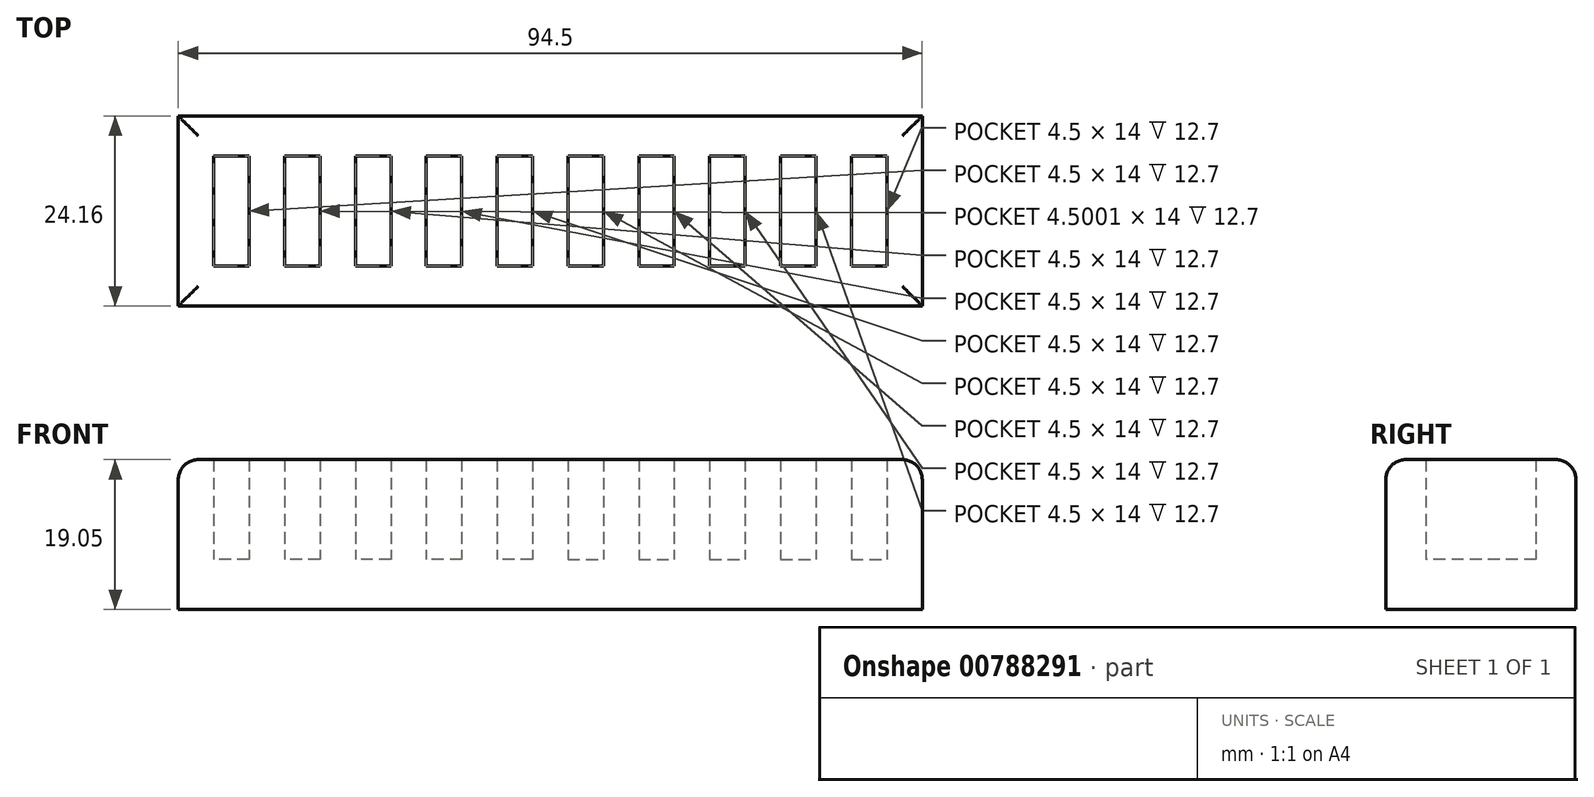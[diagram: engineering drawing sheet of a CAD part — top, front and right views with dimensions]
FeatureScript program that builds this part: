
annotation { "Feature Type Name" : "Feature", "Feature Type Description" : "" }
export const myFeature = defineFeature(function(context is Context, id is Id, definition is map)
    precondition{}
    {
        {
            var Q0;
            Q0=qCreatedBy(makeId("Top.planeOp"),FACE);
            var sketch = newSketch(context, id + "F0", { "sketchPlane" : qUnion([Q0])});
            skLineSegment(sketch, "E0.bottom", {"start": v(-24.19, 0) * mm, "end": v(-15.19, 0) * mm});
            skLineSegment(sketch, "E0.top", {"start": v(-24.19, 24.16) * mm, "end": v(-15.19, 24.16) * mm});
            skLineSegment(sketch, "E0.left", {"start": v(-24.19, 0) * mm, "end": v(-24.19, 24.16) * mm});
            skLineSegment(sketch, "E0.right", {"start": v(-15.19, 0) * mm, "end": v(-15.19, 24.16) * mm});
            skLineSegment(sketch, "E1", {"start": v(-15.19, 24.16) * mm, "end": v(-15.19, 19.08) * mm});
            skLineSegment(sketch, "E2.bottom", {"start": v(-24.19, 0) * mm, "end": v(-19.69, 0) * mm});
            skLineSegment(sketch, "E2.top", {"start": v(-24.19, 5.08) * mm, "end": v(-19.69, 5.08) * mm});
            skLineSegment(sketch, "E2.left", {"start": v(-24.19, 0) * mm, "end": v(-24.19, 5.08) * mm});
            skLineSegment(sketch, "E2.right", {"start": v(-19.69, 0) * mm, "end": v(-19.69, 5.08) * mm});
            skLineSegment(sketch, "E3.bottom", {"start": v(-19.69, 5.08) * mm, "end": v(-15.19, 5.08) * mm});
            skLineSegment(sketch, "E3.top", {"start": v(-19.69, 19.08) * mm, "end": v(-15.19, 19.08) * mm});
            skLineSegment(sketch, "E3.left", {"start": v(-19.69, 5.08) * mm, "end": v(-19.69, 19.08) * mm});
            skLineSegment(sketch, "E3.right", {"start": v(-15.19, 5.08) * mm, "end": v(-15.19, 19.08) * mm});
            skLineSegment(sketch, "E4", {"start": v(-24.19, 0) * mm, "end": v(-33.19, 0) * mm});
            skLineSegment(sketch, "E5", {"start": v(-33.19, 0) * mm, "end": v(-42.19, 0) * mm});
            skLineSegment(sketch, "E6", {"start": v(-42.19, 0) * mm, "end": v(-51.19, 0) * mm});
            skLineSegment(sketch, "E7", {"start": v(-51.19, 0) * mm, "end": v(-60.19, 0) * mm});
            skLineSegment(sketch, "E8", {"start": v(-60.19, 0) * mm, "end": v(-69.19, 0) * mm});
            skLineSegment(sketch, "E9", {"start": v(-15.19, 0) * mm, "end": v(-6.19, 0) * mm});
            skLineSegment(sketch, "E10", {"start": v(-6.19, 0) * mm, "end": v(2.81, 0) * mm});
            skLineSegment(sketch, "E11", {"start": v(2.81, 0) * mm, "end": v(11.81, 0) * mm});
            skLineSegment(sketch, "E12", {"start": v(11.81, 0) * mm, "end": v(20.81, 0) * mm});
            skLineSegment(sketch, "E13.bottom", {"start": v(-24.19, 24.16) * mm, "end": v(-33.19, 24.16) * mm});
            skLineSegment(sketch, "E13.left", {"start": v(-24.19, 24.16) * mm, "end": v(-24.19, 0) * mm});
            skLineSegment(sketch, "E13.right", {"start": v(-33.19, 24.16) * mm, "end": v(-33.19, 0) * mm});
            skLineSegment(sketch, "E14.bottom", {"start": v(-33.19, 24.16) * mm, "end": v(-42.19, 24.16) * mm});
            skLineSegment(sketch, "E14.right", {"start": v(-42.19, 24.16) * mm, "end": v(-42.19, 0) * mm});
            skLineSegment(sketch, "E15.bottom", {"start": v(-42.19, 24.16) * mm, "end": v(-51.19, 24.16) * mm});
            skLineSegment(sketch, "E15.right", {"start": v(-51.19, 24.16) * mm, "end": v(-51.19, 0) * mm});
            skLineSegment(sketch, "E16.bottom", {"start": v(-51.19, 24.16) * mm, "end": v(-60.19, 24.16) * mm});
            skLineSegment(sketch, "E16.right", {"start": v(-60.19, 24.16) * mm, "end": v(-60.19, 0) * mm});
            skLineSegment(sketch, "E17.bottom", {"start": v(-60.19, 24.16) * mm, "end": v(-69.19, 24.16) * mm});
            skLineSegment(sketch, "E17.right", {"start": v(-69.19, 24.16) * mm, "end": v(-69.19, 0) * mm});
            skLineSegment(sketch, "E18.bottom", {"start": v(-15.19, 24.16) * mm, "end": v(-6.19, 24.16) * mm});
            skLineSegment(sketch, "E18.left", {"start": v(-15.19, 24.16) * mm, "end": v(-15.19, 0) * mm});
            skLineSegment(sketch, "E18.right", {"start": v(-6.19, 24.16) * mm, "end": v(-6.19, 0) * mm});
            skLineSegment(sketch, "E19.bottom", {"start": v(-6.19, 24.16) * mm, "end": v(2.81, 24.16) * mm});
            skLineSegment(sketch, "E19.right", {"start": v(2.81, 24.16) * mm, "end": v(2.81, 0) * mm});
            skLineSegment(sketch, "E20.bottom", {"start": v(2.81, 24.16) * mm, "end": v(11.81, 24.16) * mm});
            skLineSegment(sketch, "E20.right", {"start": v(11.81, 24.16) * mm, "end": v(11.81, 0) * mm});
            skLineSegment(sketch, "E21.bottom", {"start": v(11.81, 24.16) * mm, "end": v(20.81, 24.16) * mm});
            skLineSegment(sketch, "E21.right", {"start": v(20.81, 24.16) * mm, "end": v(20.81, 0) * mm});
            skLineSegment(sketch, "E22", {"start": v(-15.19, 19.08) * mm, "end": v(-6.19, 19.08) * mm});
            skLineSegment(sketch, "E23", {"start": v(-6.19, 19.08) * mm, "end": v(2.81, 19.08) * mm});
            skLineSegment(sketch, "E24", {"start": v(2.81, 19.08) * mm, "end": v(11.81, 19.08) * mm});
            skLineSegment(sketch, "E25", {"start": v(11.81, 19.08) * mm, "end": v(20.81, 19.08) * mm});
            skLineSegment(sketch, "E26", {"start": v(-19.69, 19.08) * mm, "end": v(-33.19, 19.08) * mm});
            skLineSegment(sketch, "E27", {"start": v(-33.19, 19.08) * mm, "end": v(-42.19, 19.08) * mm});
            skLineSegment(sketch, "E28", {"start": v(-42.19, 19.08) * mm, "end": v(-51.19, 19.08) * mm});
            skLineSegment(sketch, "E29", {"start": v(-51.19, 19.08) * mm, "end": v(-60.19, 19.08) * mm});
            skLineSegment(sketch, "E30", {"start": v(-60.19, 19.08) * mm, "end": v(-69.19, 19.08) * mm});
            skLineSegment(sketch, "E31", {"start": v(-15.19, 5.08) * mm, "end": v(-6.19, 5.08) * mm});
            skLineSegment(sketch, "E32", {"start": v(-6.19, 5.08) * mm, "end": v(2.81, 5.08) * mm});
            skLineSegment(sketch, "E33", {"start": v(2.81, 5.08) * mm, "end": v(11.81, 5.08) * mm});
            skLineSegment(sketch, "E34", {"start": v(11.81, 5.08) * mm, "end": v(20.81, 5.08) * mm});
            skLineSegment(sketch, "E35", {"start": v(-24.19, 5.08) * mm, "end": v(-33.19, 5.08) * mm});
            skLineSegment(sketch, "E36", {"start": v(-33.19, 5.08) * mm, "end": v(-42.19, 5.08) * mm});
            skLineSegment(sketch, "E37", {"start": v(-42.19, 5.08) * mm, "end": v(-51.19, 5.08) * mm});
            skLineSegment(sketch, "E38", {"start": v(-51.19, 5.08) * mm, "end": v(-60.19, 5.08) * mm});
            skLineSegment(sketch, "E39", {"start": v(-60.19, 5.08) * mm, "end": v(-69.19, 5.08) * mm});
            skLineSegment(sketch, "E40.bottom", {"start": v(-60.19, 19.08) * mm, "end": v(-64.69, 19.08) * mm});
            skLineSegment(sketch, "E40.top", {"start": v(-60.19, 5.08) * mm, "end": v(-64.69, 5.08) * mm});
            skLineSegment(sketch, "E40.left", {"start": v(-60.19, 19.08) * mm, "end": v(-60.19, 5.08) * mm});
            skLineSegment(sketch, "E40.right", {"start": v(-64.69, 19.08) * mm, "end": v(-64.69, 5.08) * mm});
            skLineSegment(sketch, "E41.bottom", {"start": v(-51.19, 19.08) * mm, "end": v(-55.69, 19.08) * mm});
            skLineSegment(sketch, "E41.top", {"start": v(-51.19, 5.08) * mm, "end": v(-55.69, 5.08) * mm});
            skLineSegment(sketch, "E41.left", {"start": v(-51.19, 19.08) * mm, "end": v(-51.19, 5.08) * mm});
            skLineSegment(sketch, "E41.right", {"start": v(-55.69, 19.08) * mm, "end": v(-55.69, 5.08) * mm});
            skLineSegment(sketch, "E42.bottom", {"start": v(-42.19, 19.08) * mm, "end": v(-46.69, 19.08) * mm});
            skLineSegment(sketch, "E42.top", {"start": v(-42.19, 5.08) * mm, "end": v(-46.69, 5.08) * mm});
            skLineSegment(sketch, "E42.left", {"start": v(-42.19, 19.08) * mm, "end": v(-42.19, 5.08) * mm});
            skLineSegment(sketch, "E42.right", {"start": v(-46.69, 19.08) * mm, "end": v(-46.69, 5.08) * mm});
            skLineSegment(sketch, "E43.bottom", {"start": v(-33.19, 19.08) * mm, "end": v(-37.69, 19.08) * mm});
            skLineSegment(sketch, "E43.top", {"start": v(-33.19, 5.08) * mm, "end": v(-37.69, 5.08) * mm});
            skLineSegment(sketch, "E43.left", {"start": v(-33.19, 19.08) * mm, "end": v(-33.19, 5.08) * mm});
            skLineSegment(sketch, "E43.right", {"start": v(-37.69, 19.08) * mm, "end": v(-37.69, 5.08) * mm});
            skLineSegment(sketch, "E44.bottom", {"start": v(-24.19, 19.08) * mm, "end": v(-28.69, 19.08) * mm});
            skLineSegment(sketch, "E44.top", {"start": v(-24.19, 5.08) * mm, "end": v(-28.69, 5.08) * mm});
            skLineSegment(sketch, "E44.left", {"start": v(-24.19, 19.08) * mm, "end": v(-24.19, 5.08) * mm});
            skLineSegment(sketch, "E44.right", {"start": v(-28.69, 19.08) * mm, "end": v(-28.69, 5.08) * mm});
            skLineSegment(sketch, "E45.bottom", {"start": v(-6.19, 19.08) * mm, "end": v(-10.69, 19.08) * mm});
            skLineSegment(sketch, "E45.top", {"start": v(-6.19, 5.08) * mm, "end": v(-10.69, 5.08) * mm});
            skLineSegment(sketch, "E45.left", {"start": v(-6.19, 19.08) * mm, "end": v(-6.19, 5.08) * mm});
            skLineSegment(sketch, "E45.right", {"start": v(-10.69, 19.08) * mm, "end": v(-10.69, 5.08) * mm});
            skLineSegment(sketch, "E46.bottom", {"start": v(2.81, 19.08) * mm, "end": v(-1.69, 19.08) * mm});
            skLineSegment(sketch, "E46.top", {"start": v(2.81, 5.08) * mm, "end": v(-1.69, 5.08) * mm});
            skLineSegment(sketch, "E46.left", {"start": v(2.81, 19.08) * mm, "end": v(2.81, 5.08) * mm});
            skLineSegment(sketch, "E46.right", {"start": v(-1.69, 19.08) * mm, "end": v(-1.69, 5.08) * mm});
            skLineSegment(sketch, "E47.bottom", {"start": v(11.81, 19.08) * mm, "end": v(7.31, 19.08) * mm});
            skLineSegment(sketch, "E47.top", {"start": v(11.81, 5.08) * mm, "end": v(7.31, 5.08) * mm});
            skLineSegment(sketch, "E47.left", {"start": v(11.81, 19.08) * mm, "end": v(11.81, 5.08) * mm});
            skLineSegment(sketch, "E47.right", {"start": v(7.31, 19.08) * mm, "end": v(7.31, 5.08) * mm});
            skLineSegment(sketch, "E48.bottom", {"start": v(20.81, 19.08) * mm, "end": v(16.31, 19.08) * mm});
            skLineSegment(sketch, "E48.top", {"start": v(20.81, 5.08) * mm, "end": v(16.31, 5.08) * mm});
            skLineSegment(sketch, "E48.left", {"start": v(20.81, 19.08) * mm, "end": v(20.81, 5.08) * mm});
            skLineSegment(sketch, "E48.right", {"start": v(16.31, 19.08) * mm, "end": v(16.31, 5.08) * mm});
            skLineSegment(sketch, "E49.bottom", {"start": v(20.81, 24.16) * mm, "end": v(25.31, 24.16) * mm});
            skLineSegment(sketch, "E49.top", {"start": v(20.81, 0) * mm, "end": v(25.31, 0) * mm});
            skLineSegment(sketch, "E49.right", {"start": v(25.31, 24.16) * mm, "end": v(25.31, 0) * mm});
            skSolve(sketch);
        }
        {
            var Q0;
            {var subQ4=sQuery(id+"F0.wireOp",EDGE,"E17.bottom");Q0=makeQuery(id+"F0.imprint","IMPRINT",FACE,{"disambiguationData":[TD([[makeQuery(id+"F0.imprint","IMPRINT",EDGE,{"derivedFrom":subQ4}),1.0]])]});}
            var Q1;
            {var subQ5=sQuery(id+"F0.wireOp",EDGE,"E40.right");Q1=makeQuery(id+"F0.imprint","IMPRINT",FACE,{"disambiguationData":[TD([[makeQuery(id+"F0.imprint","IMPRINT",EDGE,{"derivedFrom":subQ5}),-1.0]])]});}
            var Q2;
            {var subQ4=sQuery(id+"F0.wireOp",EDGE,"E8");Q2=makeQuery(id+"F0.imprint","IMPRINT",FACE,{"disambiguationData":[TD([[makeQuery(id+"F0.imprint","IMPRINT",EDGE,{"derivedFrom":subQ4}),-1.0]])]});}
            var Q3;
            {var subQ1=sQuery(id+"F0.wireOp",EDGE,"E7");Q3=makeQuery(id+"F0.imprint","IMPRINT",FACE,{"disambiguationData":[TD([[makeQuery(id+"F0.imprint","IMPRINT",EDGE,{"derivedFrom":subQ1}),-1.0]])]});}
            var Q4;
            {var subQ5=sQuery(id+"F0.wireOp",EDGE,"E41.right");Q4=makeQuery(id+"F0.imprint","IMPRINT",FACE,{"disambiguationData":[TD([[makeQuery(id+"F0.imprint","IMPRINT",EDGE,{"derivedFrom":subQ5}),-1.0]])]});}
            var Q5;
            {var subQ4=sQuery(id+"F0.wireOp",EDGE,"E16.bottom");Q5=makeQuery(id+"F0.imprint","IMPRINT",FACE,{"disambiguationData":[TD([[makeQuery(id+"F0.imprint","IMPRINT",EDGE,{"derivedFrom":subQ4}),1.0]])]});}
            var Q6;
            {var subQ4=sQuery(id+"F0.wireOp",EDGE,"E15.bottom");Q6=makeQuery(id+"F0.imprint","IMPRINT",FACE,{"disambiguationData":[TD([[makeQuery(id+"F0.imprint","IMPRINT",EDGE,{"derivedFrom":subQ4}),1.0]])]});}
            var Q7;
            {var subQ5=sQuery(id+"F0.wireOp",EDGE,"E42.right");Q7=makeQuery(id+"F0.imprint","IMPRINT",FACE,{"disambiguationData":[TD([[makeQuery(id+"F0.imprint","IMPRINT",EDGE,{"derivedFrom":subQ5}),-1.0]])]});}
            var Q8;
            {var subQ1=sQuery(id+"F0.wireOp",EDGE,"E6");Q8=makeQuery(id+"F0.imprint","IMPRINT",FACE,{"disambiguationData":[TD([[makeQuery(id+"F0.imprint","IMPRINT",EDGE,{"derivedFrom":subQ1}),-1.0]])]});}
            var Q9;
            {var subQ4=sQuery(id+"F0.wireOp",EDGE,"E5");Q9=makeQuery(id+"F0.imprint","IMPRINT",FACE,{"disambiguationData":[TD([[makeQuery(id+"F0.imprint","IMPRINT",EDGE,{"derivedFrom":subQ4}),-1.0]])]});}
            var Q10;
            {var subQ5=sQuery(id+"F0.wireOp",EDGE,"E43.right");Q10=makeQuery(id+"F0.imprint","IMPRINT",FACE,{"disambiguationData":[TD([[makeQuery(id+"F0.imprint","IMPRINT",EDGE,{"derivedFrom":subQ5}),-1.0]])]});}
            var Q11;
            {var subQ1=sQuery(id+"F0.wireOp",EDGE,"E14.bottom");Q11=makeQuery(id+"F0.imprint","IMPRINT",FACE,{"disambiguationData":[TD([[makeQuery(id+"F0.imprint","IMPRINT",EDGE,{"derivedFrom":subQ1}),1.0]])]});}
            var Q12;
            {var subQ4=sQuery(id+"F0.wireOp",EDGE,"E13.bottom");Q12=makeQuery(id+"F0.imprint","IMPRINT",FACE,{"disambiguationData":[TD([[makeQuery(id+"F0.imprint","IMPRINT",EDGE,{"derivedFrom":subQ4}),1.0]])]});}
            var Q13;
            {var subQ5=sQuery(id+"F0.wireOp",EDGE,"E44.right");Q13=makeQuery(id+"F0.imprint","IMPRINT",FACE,{"disambiguationData":[TD([[makeQuery(id+"F0.imprint","IMPRINT",EDGE,{"derivedFrom":subQ5}),-1.0]])]});}
            var Q14;
            {var subQ5=sQuery(id+"F0.wireOp",EDGE,"E4");Q14=makeQuery(id+"F0.imprint","IMPRINT",FACE,{"disambiguationData":[TD([[makeQuery(id+"F0.imprint","IMPRINT",EDGE,{"derivedFrom":subQ5}),-1.0]])]});}
            var Q15;
            {var subQ0=sQuery(id+"F0.wireOp",EDGE,"E2.top");Q15=makeQuery(id+"F0.imprint","IMPRINT",FACE,{"disambiguationData":[TD([[makeQuery(id+"F0.imprint","IMPRINT",EDGE,{"derivedFrom":subQ0}),1.0]])]});}
            var Q16;
            {var subQ4=sQuery(id+"F0.wireOp",EDGE,"E2.top");Q16=makeQuery(id+"F0.imprint","IMPRINT",FACE,{"disambiguationData":[TD([[makeQuery(id+"F0.imprint","IMPRINT",EDGE,{"derivedFrom":subQ4}),-1.0]])]});}
            var Q17;
            {var subQ0=sQuery(id+"F0.wireOp",EDGE,"E2.right");Q17=makeQuery(id+"F0.imprint","IMPRINT",FACE,{"disambiguationData":[TD([[makeQuery(id+"F0.imprint","IMPRINT",EDGE,{"derivedFrom":subQ0}),-1.0]])]});}
            var Q18;
            {var subQ1=sQuery(id+"F0.wireOp",EDGE,"E0.top");Q18=makeQuery(id+"F0.imprint","IMPRINT",FACE,{"disambiguationData":[TD([[makeQuery(id+"F0.imprint","IMPRINT",EDGE,{"derivedFrom":subQ1}),-1.0]])]});}
            var Q19;
            {var subQ1=sQuery(id+"F0.wireOp",EDGE,"E9");Q19=makeQuery(id+"F0.imprint","IMPRINT",FACE,{"disambiguationData":[TD([[makeQuery(id+"F0.imprint","IMPRINT",EDGE,{"derivedFrom":subQ1}),1.0]])]});}
            var Q20;
            {var subQ5=sQuery(id+"F0.wireOp",EDGE,"E45.right");Q20=makeQuery(id+"F0.imprint","IMPRINT",FACE,{"disambiguationData":[TD([[makeQuery(id+"F0.imprint","IMPRINT",EDGE,{"derivedFrom":subQ5}),-1.0]])]});}
            var Q21;
            {var subQ4=sQuery(id+"F0.wireOp",EDGE,"E18.bottom");Q21=makeQuery(id+"F0.imprint","IMPRINT",FACE,{"disambiguationData":[TD([[makeQuery(id+"F0.imprint","IMPRINT",EDGE,{"derivedFrom":subQ4}),-1.0]])]});}
            var Q22;
            {var subQ1=sQuery(id+"F0.wireOp",EDGE,"E19.bottom");Q22=makeQuery(id+"F0.imprint","IMPRINT",FACE,{"disambiguationData":[TD([[makeQuery(id+"F0.imprint","IMPRINT",EDGE,{"derivedFrom":subQ1}),-1.0]])]});}
            var Q23;
            {var subQ5=sQuery(id+"F0.wireOp",EDGE,"E46.right");Q23=makeQuery(id+"F0.imprint","IMPRINT",FACE,{"disambiguationData":[TD([[makeQuery(id+"F0.imprint","IMPRINT",EDGE,{"derivedFrom":subQ5}),-1.0]])]});}
            var Q24;
            {var subQ1=sQuery(id+"F0.wireOp",EDGE,"E10");Q24=makeQuery(id+"F0.imprint","IMPRINT",FACE,{"disambiguationData":[TD([[makeQuery(id+"F0.imprint","IMPRINT",EDGE,{"derivedFrom":subQ1}),1.0]])]});}
            var Q25;
            {var subQ4=sQuery(id+"F0.wireOp",EDGE,"E11");Q25=makeQuery(id+"F0.imprint","IMPRINT",FACE,{"disambiguationData":[TD([[makeQuery(id+"F0.imprint","IMPRINT",EDGE,{"derivedFrom":subQ4}),1.0]])]});}
            var Q26;
            {var subQ5=sQuery(id+"F0.wireOp",EDGE,"E47.right");Q26=makeQuery(id+"F0.imprint","IMPRINT",FACE,{"disambiguationData":[TD([[makeQuery(id+"F0.imprint","IMPRINT",EDGE,{"derivedFrom":subQ5}),-1.0]])]});}
            var Q27;
            {var subQ5=sQuery(id+"F0.wireOp",EDGE,"E20.bottom");Q27=makeQuery(id+"F0.imprint","IMPRINT",FACE,{"disambiguationData":[TD([[makeQuery(id+"F0.imprint","IMPRINT",EDGE,{"derivedFrom":subQ5}),-1.0]])]});}
            var Q28;
            {var subQ1=sQuery(id+"F0.wireOp",EDGE,"E21.bottom");Q28=makeQuery(id+"F0.imprint","IMPRINT",FACE,{"disambiguationData":[TD([[makeQuery(id+"F0.imprint","IMPRINT",EDGE,{"derivedFrom":subQ1}),-1.0]])]});}
            var Q29;
            {var subQ5=sQuery(id+"F0.wireOp",EDGE,"E48.right");Q29=makeQuery(id+"F0.imprint","IMPRINT",FACE,{"disambiguationData":[TD([[makeQuery(id+"F0.imprint","IMPRINT",EDGE,{"derivedFrom":subQ5}),-1.0]])]});}
            var Q30;
            {var subQ4=sQuery(id+"F0.wireOp",EDGE,"E12");Q30=makeQuery(id+"F0.imprint","IMPRINT",FACE,{"disambiguationData":[TD([[makeQuery(id+"F0.imprint","IMPRINT",EDGE,{"derivedFrom":subQ4}),1.0]])]});}
            var Q31;
            {var subQ0=sQuery(id+"F0.wireOp",EDGE,"E49.bottom");Q31=makeQuery(id+"F0.imprint","IMPRINT",FACE,{"disambiguationData":[TD([[makeQuery(id+"F0.imprint","IMPRINT",EDGE,{"derivedFrom":subQ0}),-1.0]])]});}
            extrude(context, id + "F1", {"entities" : qUnion([Q0, Q1, Q2, Q3, Q4, Q5, Q6, Q7, Q8, Q9, Q10, Q11, Q12, Q13, Q14, Q15, Q16, Q17, Q18, Q19, Q20, Q21, Q22, Q23, Q24, Q25, Q26, Q27, Q28, Q29, Q30, Q31]), "depth" : 12.7 * mm, "offsetDistance" : 25.4 * mm});
        }
        {
            var Q0;
            Q0=makeQuery(id+"F1.opExtrude","CAP_FACE",FACE,{"disambiguationData":[OSD([sQuery(id+"F0.wireOp",EDGE,"E0.bottom"),sQuery(id+"F0.wireOp",EDGE,"E0.top"),sQuery(id+"F0.wireOp",EDGE,"E0.left"),sQuery(id+"F0.wireOp",EDGE,"E0.right"),sQuery(id+"F0.wireOp",EDGE,"E3.bottom"),sQuery(id+"F0.wireOp",EDGE,"E3.top"),sQuery(id+"F0.wireOp",EDGE,"E3.left"),sQuery(id+"F0.wireOp",EDGE,"E4"),sQuery(id+"F0.wireOp",EDGE,"E5"),sQuery(id+"F0.wireOp",EDGE,"E6"),sQuery(id+"F0.wireOp",EDGE,"E7"),sQuery(id+"F0.wireOp",EDGE,"E8"),sQuery(id+"F0.wireOp",EDGE,"E9"),sQuery(id+"F0.wireOp",EDGE,"E10"),sQuery(id+"F0.wireOp",EDGE,"E11"),sQuery(id+"F0.wireOp",EDGE,"E12"),sQuery(id+"F0.wireOp",EDGE,"E13.bottom"),sQuery(id+"F0.wireOp",EDGE,"E13.right"),sQuery(id+"F0.wireOp",EDGE,"E14.bottom"),sQuery(id+"F0.wireOp",EDGE,"E14.right"),sQuery(id+"F0.wireOp",EDGE,"E15.bottom"),sQuery(id+"F0.wireOp",EDGE,"E15.right"),sQuery(id+"F0.wireOp",EDGE,"E16.bottom"),sQuery(id+"F0.wireOp",EDGE,"E16.right"),sQuery(id+"F0.wireOp",EDGE,"E17.bottom"),sQuery(id+"F0.wireOp",EDGE,"E17.right"),sQuery(id+"F0.wireOp",EDGE,"E18.bottom"),sQuery(id+"F0.wireOp",EDGE,"E18.right"),sQuery(id+"F0.wireOp",EDGE,"E19.bottom"),sQuery(id+"F0.wireOp",EDGE,"E19.right"),sQuery(id+"F0.wireOp",EDGE,"E20.bottom"),sQuery(id+"F0.wireOp",EDGE,"E20.right"),sQuery(id+"F0.wireOp",EDGE,"E21.bottom"),sQuery(id+"F0.wireOp",EDGE,"E21.right"),sQuery(id+"F0.wireOp",EDGE,"E22"),sQuery(id+"F0.wireOp",EDGE,"E23"),sQuery(id+"F0.wireOp",EDGE,"E24"),sQuery(id+"F0.wireOp",EDGE,"E25"),sQuery(id+"F0.wireOp",EDGE,"E26"),sQuery(id+"F0.wireOp",EDGE,"E27"),sQuery(id+"F0.wireOp",EDGE,"E28"),sQuery(id+"F0.wireOp",EDGE,"E29"),sQuery(id+"F0.wireOp",EDGE,"E30"),sQuery(id+"F0.wireOp",EDGE,"E31"),sQuery(id+"F0.wireOp",EDGE,"E32"),sQuery(id+"F0.wireOp",EDGE,"E33"),sQuery(id+"F0.wireOp",EDGE,"E34"),sQuery(id+"F0.wireOp",EDGE,"E35"),sQuery(id+"F0.wireOp",EDGE,"E36"),sQuery(id+"F0.wireOp",EDGE,"E37"),sQuery(id+"F0.wireOp",EDGE,"E38"),sQuery(id+"F0.wireOp",EDGE,"E39"),sQuery(id+"F0.wireOp",EDGE,"E40.right"),sQuery(id+"F0.wireOp",EDGE,"E41.right"),sQuery(id+"F0.wireOp",EDGE,"E42.right"),sQuery(id+"F0.wireOp",EDGE,"E43.right"),sQuery(id+"F0.wireOp",EDGE,"E44.right"),sQuery(id+"F0.wireOp",EDGE,"E45.right"),sQuery(id+"F0.wireOp",EDGE,"E46.right"),sQuery(id+"F0.wireOp",EDGE,"E47.right"),sQuery(id+"F0.wireOp",EDGE,"E48.right"),sQuery(id+"F0.wireOp",EDGE,"E49.bottom"),sQuery(id+"F0.wireOp",EDGE,"E49.top"),sQuery(id+"F0.wireOp",EDGE,"E49.right")])],"isStart":true});
            var sketch = newSketch(context, id + "F2", { "sketchPlane" : qUnion([Q0])});
            skLineSegment(sketch, "E50.bottom", {"start": v(-69.19, 0) * mm, "end": v(25.31, 0) * mm});
            skLineSegment(sketch, "E50.top", {"start": v(-69.19, -24.16) * mm, "end": v(25.31, -24.16) * mm});
            skLineSegment(sketch, "E50.left", {"start": v(-69.19, 0) * mm, "end": v(-69.19, -24.16) * mm});
            skLineSegment(sketch, "E50.right", {"start": v(25.31, 0) * mm, "end": v(25.31, -24.16) * mm});
            skSolve(sketch);
        }
        {
            var Q0;
            Q0=qSketchRegion(id+"F2",true);
            extrude(context, id + "F3", {"entities" : qUnion([Q0]), "operationType" : NewBodyOperationType.ADD, "depth" : 6.35 * mm, "offsetDistance" : 25.4 * mm});
        }
        {
            var Q0;
            Q0=makeQuery(id+"F1.opExtrude","CAP_EDGE",EDGE,{"disambiguationData":[OSD([sQuery(id+"F0.wireOp",EDGE,"E0.top"),sQuery(id+"F0.wireOp",EDGE,"E13.bottom"),sQuery(id+"F0.wireOp",EDGE,"E14.bottom"),sQuery(id+"F0.wireOp",EDGE,"E15.bottom"),sQuery(id+"F0.wireOp",EDGE,"E16.bottom"),sQuery(id+"F0.wireOp",EDGE,"E17.bottom"),sQuery(id+"F0.wireOp",EDGE,"E18.bottom"),sQuery(id+"F0.wireOp",EDGE,"E19.bottom"),sQuery(id+"F0.wireOp",EDGE,"E20.bottom"),sQuery(id+"F0.wireOp",EDGE,"E21.bottom"),sQuery(id+"F0.wireOp",EDGE,"E49.bottom")])],"isStart":false});
            var Q1;
            Q1=makeQuery(id+"F1.opExtrude","CAP_EDGE",EDGE,{"disambiguationData":[OSD([sQuery(id+"F0.wireOp",EDGE,"E0.bottom"),sQuery(id+"F0.wireOp",EDGE,"E4"),sQuery(id+"F0.wireOp",EDGE,"E5"),sQuery(id+"F0.wireOp",EDGE,"E6"),sQuery(id+"F0.wireOp",EDGE,"E7"),sQuery(id+"F0.wireOp",EDGE,"E8"),sQuery(id+"F0.wireOp",EDGE,"E9"),sQuery(id+"F0.wireOp",EDGE,"E10"),sQuery(id+"F0.wireOp",EDGE,"E11"),sQuery(id+"F0.wireOp",EDGE,"E12"),sQuery(id+"F0.wireOp",EDGE,"E49.top")])],"isStart":false});
            var Q2;
            Q2=makeQuery(id+"F1.opExtrude","CAP_EDGE",EDGE,{"disambiguationData":[OSD([sQuery(id+"F0.wireOp",EDGE,"E17.right")])],"isStart":false});
            var Q3;
            Q3=makeQuery(id+"F1.opExtrude","CAP_EDGE",EDGE,{"disambiguationData":[OSD([sQuery(id+"F0.wireOp",EDGE,"E49.right")])],"isStart":false});
            fillet(context, id + "F4", {"entities" : qUnion([Q0, Q1, Q2, Q3]), "radius" : 2.54 * mm, "tangentPropagation" : true, "allowEdgeOverflow" : false});
        }
    });
